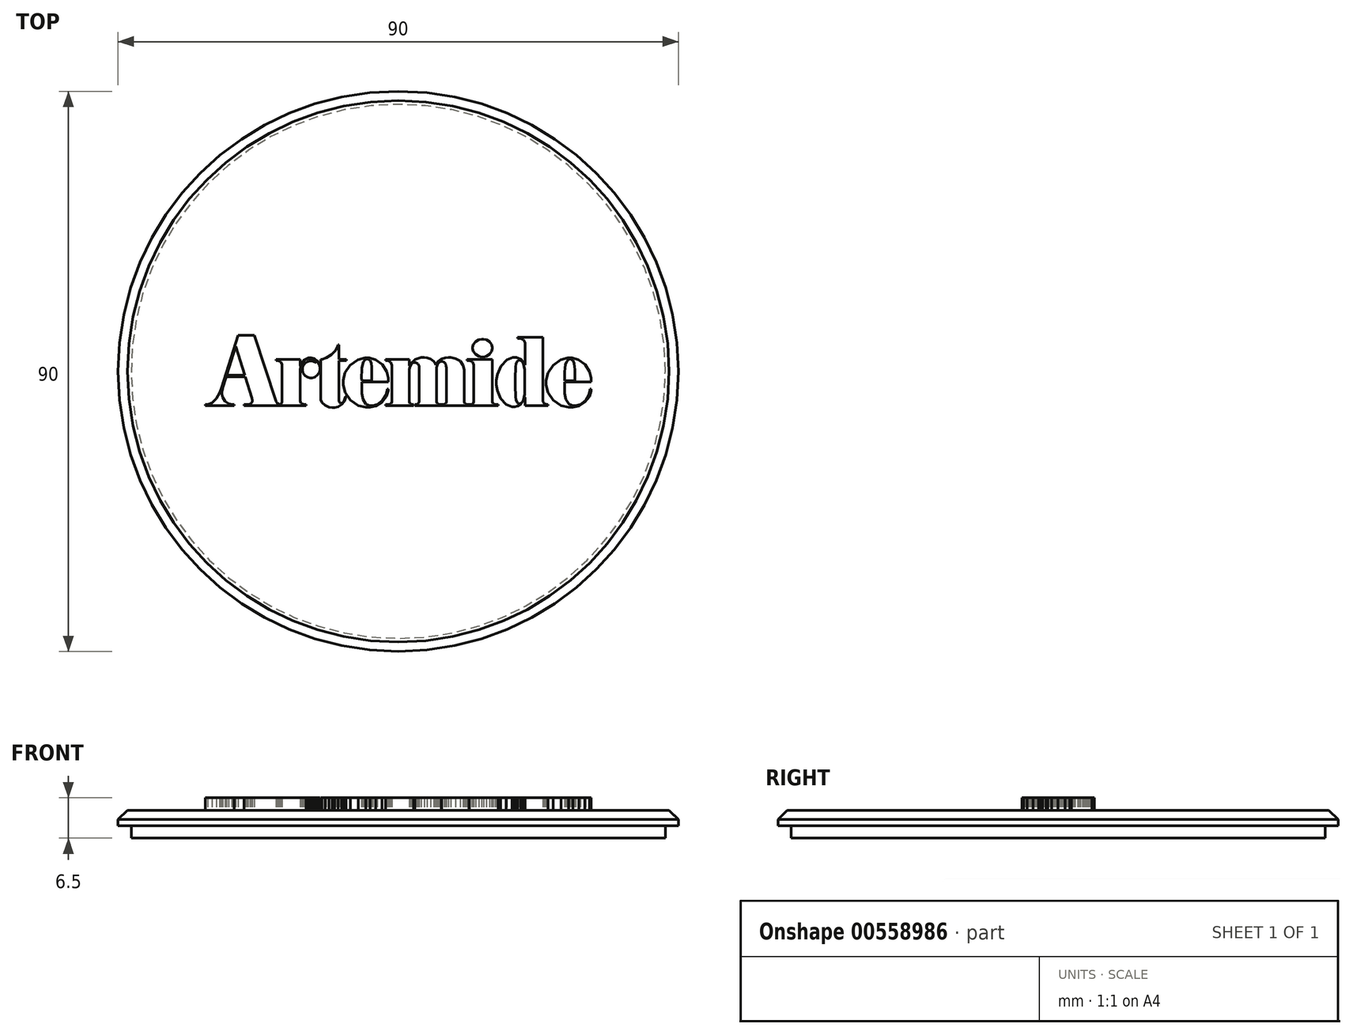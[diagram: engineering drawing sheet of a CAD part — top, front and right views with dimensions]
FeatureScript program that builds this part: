
annotation { "Feature Type Name" : "Feature", "Feature Type Description" : "" }
export const myFeature = defineFeature(function(context is Context, id is Id, definition is map)
    precondition{}
    {
        {
            var Q0;
            Q0=qCreatedBy(makeId("Top.planeOp"),FACE);
            var sketch = newSketch(context, id + "F0", { "sketchPlane" : qUnion([Q0])});
            skCircle(sketch, "E0", {"center": v(0, 0) * mm, "radius": 42.9 * mm});
            skSolve(sketch);
        }
        {
            var Q0;
            Q0 = qSketchRegion(id + "F0", true);
            extrude(context, id + "F1", {"entities" : qUnion([Q0]), "depth" : 2 * mm, "offsetDistance" : 25 * mm});
        }
        {
            var Q0;
            Q0=makeQuery(id+"F1.opExtrude","CAP_FACE",FACE,{"disambiguationData":[OSD([sQuery(id+"F0.wireOp",EDGE,"E0")])],"isStart":false});
            var sketch = newSketch(context, id + "F2", { "sketchPlane" : qUnion([Q0])});
            skCircle(sketch, "E1", {"center": v(0, 0) * mm, "radius": 45 * mm});
            skSolve(sketch);
        }
        {
            var Q0;
            Q0=makeQuery(id+"F2.imprint","IMPRINT",FACE,{"disambiguationData":[TD([[makeQuery(id+"F2.imprint","IMPRINT",EDGE,{"derivedFrom":sQuery(id+"F2.wireOp",EDGE,"E1")}),1.0]])]});
            var Q1;
            Q1=makeQuery(id+"F2.imprint","IMPRINT",FACE,{"disambiguationData":[TD([[makeQuery(id+"F2.imprint","IMPRINT",EDGE,{"derivedFrom":makeQuery(id+"F1.opExtrude","CAP_EDGE",EDGE,{"disambiguationData":[OSD([sQuery(id+"F0.wireOp",EDGE,"E0")])],"isStart":false})}),1.0]])]});
            extrude(context, id + "F3", {"entities" : qUnion([Q0, Q1]), "operationType" : NewBodyOperationType.ADD, "depth" : 2.5 * mm, "offsetDistance" : 25 * mm});
        }
        {
            var Q0;
            Q0=makeQuery(id+"F3.opExtrude","CAP_EDGE",EDGE,{"disambiguationData":[OSD([sQuery(id+"F2.wireOp",EDGE,"E1")])],"isStart":false});
            chamfer(context, id + "F4", {"entities" : qUnion([Q0]), "width" : 1.5 * mm, "tangentPropagation" : true});
        }
        {
            var Q0;
            Q0=makeQuery(id+"F3.opExtrude","CAP_FACE",FACE,{"disambiguationData":[OSD([sQuery(id+"F2.wireOp",EDGE,"E1")])],"isStart":false});
            var sketch = newSketch(context, id + "F5", { "sketchPlane" : qUnion([Q0])});
            skLineSegment(sketch, "E2", {"start": v(11.36, -5.33) * mm, "end": v(11.36, -5.52) * mm});
            skLineSegment(sketch, "E3", {"start": v(11.36, -5.52) * mm, "end": v(7, -5.52) * mm});
            skLineSegment(sketch, "E4", {"start": v(7, -5.52) * mm, "end": v(7, -5.33) * mm});
            skLineSegment(sketch, "E5", {"start": v(7, -5.33) * mm, "end": v(7.24, -5.33) * mm});
            skLineSegment(sketch, "E6", {"start": v(7.24, -5.33) * mm, "end": v(7.33, -5.33) * mm});
            skLineSegment(sketch, "E7", {"start": v(7.33, -5.33) * mm, "end": v(7.6, -5.2) * mm});
            skLineSegment(sketch, "E8", {"start": v(7.6, -5.2) * mm, "end": v(7.73, -4.93) * mm});
            skLineSegment(sketch, "E9", {"start": v(7.73, -4.93) * mm, "end": v(7.73, -4.84) * mm});
            skLineSegment(sketch, "E10", {"start": v(7.73, -4.84) * mm, "end": v(7.73, 0.46) * mm});
            skLineSegment(sketch, "E11", {"start": v(7.73, 0.46) * mm, "end": v(7.73, 0.56) * mm});
            skLineSegment(sketch, "E12", {"start": v(7.73, 0.56) * mm, "end": v(7.7, 0.85) * mm});
            skLineSegment(sketch, "E13", {"start": v(7.7, 0.85) * mm, "end": v(7.58, 1.21) * mm});
            skLineSegment(sketch, "E14", {"start": v(7.58, 1.21) * mm, "end": v(7.35, 1.48) * mm});
            skLineSegment(sketch, "E15", {"start": v(7.35, 1.48) * mm, "end": v(7.07, 1.58) * mm});
            skLineSegment(sketch, "E16", {"start": v(7.07, 1.58) * mm, "end": v(6.97, 1.58) * mm});
            skLineSegment(sketch, "E17", {"start": v(6.97, 1.58) * mm, "end": v(6.88, 1.58) * mm});
            skLineSegment(sketch, "E18", {"start": v(6.88, 1.58) * mm, "end": v(6.58, 1.48) * mm});
            skLineSegment(sketch, "E19", {"start": v(6.58, 1.48) * mm, "end": v(6.34, 1.21) * mm});
            skLineSegment(sketch, "E20", {"start": v(6.34, 1.21) * mm, "end": v(6.21, 0.85) * mm});
            skLineSegment(sketch, "E21", {"start": v(6.21, 0.85) * mm, "end": v(6.18, 0.56) * mm});
            skLineSegment(sketch, "E22", {"start": v(6.18, 0.56) * mm, "end": v(6.18, 0.46) * mm});
            skLineSegment(sketch, "E23", {"start": v(6.18, 0.46) * mm, "end": v(6.18, -4.74) * mm});
            skLineSegment(sketch, "E24", {"start": v(6.18, -4.74) * mm, "end": v(6.18, -4.85) * mm});
            skLineSegment(sketch, "E25", {"start": v(6.18, -4.85) * mm, "end": v(6.3, -5.17) * mm});
            skLineSegment(sketch, "E26", {"start": v(6.3, -5.17) * mm, "end": v(6.6, -5.33) * mm});
            skLineSegment(sketch, "E27", {"start": v(6.6, -5.33) * mm, "end": v(6.69, -5.33) * mm});
            skLineSegment(sketch, "E28", {"start": v(6.69, -5.33) * mm, "end": v(6.9, -5.33) * mm});
            skLineSegment(sketch, "E29", {"start": v(6.9, -5.33) * mm, "end": v(6.9, -5.52) * mm});
            skLineSegment(sketch, "E30", {"start": v(6.9, -5.52) * mm, "end": v(2.65, -5.52) * mm});
            skLineSegment(sketch, "E31", {"start": v(2.65, -5.52) * mm, "end": v(2.65, -5.33) * mm});
            skLineSegment(sketch, "E32", {"start": v(2.65, -5.33) * mm, "end": v(2.94, -5.33) * mm});
            skLineSegment(sketch, "E33", {"start": v(2.94, -5.33) * mm, "end": v(3.02, -5.33) * mm});
            skLineSegment(sketch, "E34", {"start": v(3.02, -5.33) * mm, "end": v(3.26, -5.14) * mm});
            skLineSegment(sketch, "E35", {"start": v(3.26, -5.14) * mm, "end": v(3.32, -4.84) * mm});
            skLineSegment(sketch, "E36", {"start": v(3.32, -4.84) * mm, "end": v(3.32, -4.74) * mm});
            skLineSegment(sketch, "E37", {"start": v(3.32, -4.74) * mm, "end": v(3.32, 0.68) * mm});
            skLineSegment(sketch, "E38", {"start": v(3.32, 0.68) * mm, "end": v(3.32, 0.81) * mm});
            skLineSegment(sketch, "E39", {"start": v(3.32, 0.81) * mm, "end": v(3.15, 1.2) * mm});
            skLineSegment(sketch, "E40", {"start": v(3.15, 1.2) * mm, "end": v(2.8, 1.44) * mm});
            skLineSegment(sketch, "E41", {"start": v(2.8, 1.44) * mm, "end": v(2.67, 1.44) * mm});
            skLineSegment(sketch, "E42", {"start": v(2.67, 1.44) * mm, "end": v(2.57, 1.44) * mm});
            skLineSegment(sketch, "E43", {"start": v(2.57, 1.44) * mm, "end": v(2.27, 1.32) * mm});
            skLineSegment(sketch, "E44", {"start": v(2.27, 1.32) * mm, "end": v(2, 1.01) * mm});
            skLineSegment(sketch, "E45", {"start": v(2, 1.01) * mm, "end": v(1.84, 0.61) * mm});
            skLineSegment(sketch, "E46", {"start": v(1.84, 0.61) * mm, "end": v(1.8, 0.3) * mm});
            skLineSegment(sketch, "E47", {"start": v(1.8, 0.3) * mm, "end": v(1.8, 0.2) * mm});
            skLineSegment(sketch, "E48", {"start": v(1.8, 0.2) * mm, "end": v(1.8, -4.74) * mm});
            skLineSegment(sketch, "E49", {"start": v(1.8, -4.74) * mm, "end": v(1.8, -4.85) * mm});
            skLineSegment(sketch, "E50", {"start": v(1.8, -4.85) * mm, "end": v(1.9, -5.16) * mm});
            skLineSegment(sketch, "E51", {"start": v(1.9, -5.16) * mm, "end": v(2.19, -5.33) * mm});
            skLineSegment(sketch, "E52", {"start": v(2.19, -5.33) * mm, "end": v(2.28, -5.33) * mm});
            skLineSegment(sketch, "E53", {"start": v(2.28, -5.33) * mm, "end": v(2.47, -5.33) * mm});
            skLineSegment(sketch, "E54", {"start": v(2.47, -5.33) * mm, "end": v(2.47, -5.52) * mm});
            skLineSegment(sketch, "E55", {"start": v(2.47, -5.52) * mm, "end": v(-2.02, -5.52) * mm});
            skLineSegment(sketch, "E56", {"start": v(-2.02, -5.52) * mm, "end": v(-2.02, -5.33) * mm});
            skLineSegment(sketch, "E57", {"start": v(-2.02, -5.33) * mm, "end": v(-1.57, -5.33) * mm});
            skLineSegment(sketch, "E58", {"start": v(-1.57, -5.33) * mm, "end": v(-1.46, -5.33) * mm});
            skLineSegment(sketch, "E59", {"start": v(-1.46, -5.33) * mm, "end": v(-1.13, -5.18) * mm});
            skLineSegment(sketch, "E60", {"start": v(-1.13, -5.18) * mm, "end": v(-1, -4.85) * mm});
            skLineSegment(sketch, "E61", {"start": v(-1, -4.85) * mm, "end": v(-1, -4.74) * mm});
            skLineSegment(sketch, "E62", {"start": v(-1, -4.74) * mm, "end": v(-1, 0.8) * mm});
            skLineSegment(sketch, "E63", {"start": v(-1, 0.8) * mm, "end": v(-1, 0.97) * mm});
            skLineSegment(sketch, "E64", {"start": v(-1, 0.97) * mm, "end": v(-1.2, 1.47) * mm});
            skLineSegment(sketch, "E65", {"start": v(-1.2, 1.47) * mm, "end": v(-1.66, 1.72) * mm});
            skLineSegment(sketch, "E66", {"start": v(-1.66, 1.72) * mm, "end": v(-1.82, 1.72) * mm});
            skLineSegment(sketch, "E67", {"start": v(-1.82, 1.72) * mm, "end": v(-2.02, 1.72) * mm});
            skLineSegment(sketch, "E68", {"start": v(-2.02, 1.72) * mm, "end": v(-2.02, 1.9) * mm});
            skLineSegment(sketch, "E69", {"start": v(-2.02, 1.9) * mm, "end": v(1.8, 1.9) * mm});
            skLineSegment(sketch, "E70", {"start": v(1.8, 1.9) * mm, "end": v(1.8, 0.93) * mm});
            skLineSegment(sketch, "E71", {"start": v(1.8, 0.93) * mm, "end": v(1.9, 1.15) * mm});
            skLineSegment(sketch, "E72", {"start": v(1.9, 1.15) * mm, "end": v(2.7, 1.9) * mm});
            skLineSegment(sketch, "E73", {"start": v(2.7, 1.9) * mm, "end": v(3.67, 2.21) * mm});
            skLineSegment(sketch, "E74", {"start": v(3.67, 2.21) * mm, "end": v(4, 2.21) * mm});
            skLineSegment(sketch, "E75", {"start": v(4, 2.21) * mm, "end": v(4.16, 2.21) * mm});
            skLineSegment(sketch, "E76", {"start": v(4.16, 2.21) * mm, "end": v(4.64, 2.16) * mm});
            skLineSegment(sketch, "E77", {"start": v(4.64, 2.16) * mm, "end": v(5.23, 1.97) * mm});
            skLineSegment(sketch, "E78", {"start": v(5.23, 1.97) * mm, "end": v(5.7, 1.61) * mm});
            skLineSegment(sketch, "E79", {"start": v(5.7, 1.61) * mm, "end": v(5.97, 1.2) * mm});
            skLineSegment(sketch, "E80", {"start": v(5.97, 1.2) * mm, "end": v(6.02, 1.05) * mm});
            skLineSegment(sketch, "E81", {"start": v(6.02, 1.05) * mm, "end": v(6.08, 1.2) * mm});
            skLineSegment(sketch, "E82", {"start": v(6.08, 1.2) * mm, "end": v(6.4, 1.6) * mm});
            skLineSegment(sketch, "E83", {"start": v(6.4, 1.6) * mm, "end": v(6.9, 1.96) * mm});
            skLineSegment(sketch, "E84", {"start": v(6.9, 1.96) * mm, "end": v(7.52, 2.16) * mm});
            skLineSegment(sketch, "E85", {"start": v(7.52, 2.16) * mm, "end": v(8.03, 2.21) * mm});
            skLineSegment(sketch, "E86", {"start": v(8.03, 2.21) * mm, "end": v(8.2, 2.21) * mm});
            skLineSegment(sketch, "E87", {"start": v(8.2, 2.21) * mm, "end": v(8.45, 2.21) * mm});
            skLineSegment(sketch, "E88", {"start": v(8.45, 2.21) * mm, "end": v(9.19, 2.08) * mm});
            skLineSegment(sketch, "E89", {"start": v(9.19, 2.08) * mm, "end": v(9.94, 1.67) * mm});
            skLineSegment(sketch, "E90", {"start": v(9.94, 1.67) * mm, "end": v(10.43, 0.98) * mm});
            skLineSegment(sketch, "E91", {"start": v(10.43, 0.98) * mm, "end": v(10.6, 0.25) * mm});
            skLineSegment(sketch, "E92", {"start": v(10.6, 0.25) * mm, "end": v(10.6, 0) * mm});
            skLineSegment(sketch, "E93", {"start": v(10.6, 0) * mm, "end": v(10.6, -4.84) * mm});
            skLineSegment(sketch, "E94", {"start": v(10.6, -4.84) * mm, "end": v(10.6, -4.93) * mm});
            skLineSegment(sketch, "E95", {"start": v(10.6, -4.93) * mm, "end": v(10.73, -5.18) * mm});
            skLineSegment(sketch, "E96", {"start": v(10.73, -5.18) * mm, "end": v(10.97, -5.33) * mm});
            skLineSegment(sketch, "E97", {"start": v(10.97, -5.33) * mm, "end": v(11.05, -5.33) * mm});
            skLineSegment(sketch, "E98", {"start": v(11.05, -5.33) * mm, "end": v(11.36, -5.33) * mm});
            skLineSegment(sketch, "E99", {"start": v(11.42, -5.33) * mm, "end": v(11.7, -5.33) * mm});
            skLineSegment(sketch, "E100", {"start": v(11.7, -5.33) * mm, "end": v(11.8, -5.33) * mm});
            skLineSegment(sketch, "E101", {"start": v(11.8, -5.33) * mm, "end": v(12.07, -5.12) * mm});
            skLineSegment(sketch, "E102", {"start": v(12.07, -5.12) * mm, "end": v(12.13, -4.79) * mm});
            skLineSegment(sketch, "E103", {"start": v(12.13, -4.79) * mm, "end": v(12.13, -4.68) * mm});
            skLineSegment(sketch, "E104", {"start": v(12.13, -4.68) * mm, "end": v(12.13, 0.85) * mm});
            skLineSegment(sketch, "E105", {"start": v(12.13, 0.85) * mm, "end": v(12.13, 1.02) * mm});
            skLineSegment(sketch, "E106", {"start": v(12.13, 1.02) * mm, "end": v(11.95, 1.52) * mm});
            skLineSegment(sketch, "E107", {"start": v(11.95, 1.52) * mm, "end": v(11.46, 1.72) * mm});
            skLineSegment(sketch, "E108", {"start": v(11.46, 1.72) * mm, "end": v(11.3, 1.72) * mm});
            skLineSegment(sketch, "E109", {"start": v(11.3, 1.72) * mm, "end": v(11.05, 1.72) * mm});
            skLineSegment(sketch, "E110", {"start": v(11.05, 1.72) * mm, "end": v(11.05, 1.9) * mm});
            skLineSegment(sketch, "E111", {"start": v(11.05, 1.9) * mm, "end": v(15.13, 1.9) * mm});
            skLineSegment(sketch, "E112", {"start": v(15.13, 1.9) * mm, "end": v(15.13, -4.74) * mm});
            skLineSegment(sketch, "E113", {"start": v(15.13, -4.74) * mm, "end": v(15.13, -4.85) * mm});
            skLineSegment(sketch, "E114", {"start": v(15.13, -4.85) * mm, "end": v(15.25, -5.17) * mm});
            skLineSegment(sketch, "E115", {"start": v(15.25, -5.17) * mm, "end": v(15.56, -5.33) * mm});
            skLineSegment(sketch, "E116", {"start": v(15.56, -5.33) * mm, "end": v(15.66, -5.33) * mm});
            skLineSegment(sketch, "E117", {"start": v(15.66, -5.33) * mm, "end": v(16.07, -5.33) * mm});
            skLineSegment(sketch, "E118", {"start": v(16.07, -5.33) * mm, "end": v(16.07, -5.52) * mm});
            skLineSegment(sketch, "E119", {"start": v(16.07, -5.52) * mm, "end": v(11.42, -5.52) * mm});
            skLineSegment(sketch, "E120", {"start": v(11.42, -5.52) * mm, "end": v(11.42, -5.33) * mm});
            skLineSegment(sketch, "E121", {"start": v(-12.48, 1.9) * mm, "end": v(-12.25, 1.95) * mm});
            skLineSegment(sketch, "E122", {"start": v(-12.25, 1.95) * mm, "end": v(-11.57, 2.2) * mm});
            skLineSegment(sketch, "E123", {"start": v(-11.57, 2.2) * mm, "end": v(-10.73, 2.7) * mm});
            skLineSegment(sketch, "E124", {"start": v(-10.73, 2.7) * mm, "end": v(-10.06, 3.4) * mm});
            skLineSegment(sketch, "E125", {"start": v(-10.06, 3.4) * mm, "end": v(-9.74, 4.06) * mm});
            skLineSegment(sketch, "E126", {"start": v(-9.74, 4.06) * mm, "end": v(-9.69, 4.3) * mm});
            skLineSegment(sketch, "E127", {"start": v(-9.69, 4.3) * mm, "end": v(-9.55, 4.3) * mm});
            skLineSegment(sketch, "E128", {"start": v(-9.55, 4.3) * mm, "end": v(-9.55, 1.9) * mm});
            skLineSegment(sketch, "E129", {"start": v(-9.55, 1.9) * mm, "end": v(-8.3, 1.9) * mm});
            skLineSegment(sketch, "E130", {"start": v(-8.3, 1.9) * mm, "end": v(-8.3, 1.72) * mm});
            skLineSegment(sketch, "E131", {"start": v(-8.3, 1.72) * mm, "end": v(-9.55, 1.72) * mm});
            skLineSegment(sketch, "E132", {"start": v(-9.55, 1.72) * mm, "end": v(-9.55, -4.6) * mm});
            skLineSegment(sketch, "E133", {"start": v(-9.55, -4.6) * mm, "end": v(-9.55, -4.69) * mm});
            skLineSegment(sketch, "E134", {"start": v(-9.55, -4.69) * mm, "end": v(-9.48, -4.95) * mm});
            skLineSegment(sketch, "E135", {"start": v(-9.48, -4.95) * mm, "end": v(-9.27, -5.13) * mm});
            skLineSegment(sketch, "E136", {"start": v(-9.27, -5.13) * mm, "end": v(-9.2, -5.13) * mm});
            skLineSegment(sketch, "E137", {"start": v(-9.2, -5.13) * mm, "end": v(-9.13, -5.13) * mm});
            skLineSegment(sketch, "E138", {"start": v(-9.13, -5.13) * mm, "end": v(-8.9, -5.01) * mm});
            skLineSegment(sketch, "E139", {"start": v(-8.9, -5.01) * mm, "end": v(-8.72, -4.73) * mm});
            skLineSegment(sketch, "E140", {"start": v(-8.72, -4.73) * mm, "end": v(-8.6, -4.38) * mm});
            skLineSegment(sketch, "E141", {"start": v(-8.6, -4.38) * mm, "end": v(-8.54, -4.15) * mm});
            skLineSegment(sketch, "E142", {"start": v(-8.54, -4.15) * mm, "end": v(-8.53, -4.07) * mm});
            skLineSegment(sketch, "E143", {"start": v(-8.53, -4.07) * mm, "end": v(-8.4, -4.07) * mm});
            skLineSegment(sketch, "E144", {"start": v(-8.4, -4.07) * mm, "end": v(-8.44, -4.25) * mm});
            skLineSegment(sketch, "E145", {"start": v(-8.44, -4.25) * mm, "end": v(-8.65, -4.78) * mm});
            skLineSegment(sketch, "E146", {"start": v(-8.65, -4.78) * mm, "end": v(-9.07, -5.33) * mm});
            skLineSegment(sketch, "E147", {"start": v(-9.07, -5.33) * mm, "end": v(-9.66, -5.7) * mm});
            skLineSegment(sketch, "E148", {"start": v(-9.66, -5.7) * mm, "end": v(-10.23, -5.82) * mm});
            skLineSegment(sketch, "E149", {"start": v(-10.23, -5.82) * mm, "end": v(-10.42, -5.82) * mm});
            skLineSegment(sketch, "E150", {"start": v(-10.42, -5.82) * mm, "end": v(-10.6, -5.82) * mm});
            skLineSegment(sketch, "E151", {"start": v(-10.6, -5.82) * mm, "end": v(-11.1, -5.73) * mm});
            skLineSegment(sketch, "E152", {"start": v(-11.1, -5.73) * mm, "end": v(-11.77, -5.47) * mm});
            skLineSegment(sketch, "E153", {"start": v(-11.77, -5.47) * mm, "end": v(-12.28, -5.01) * mm});
            skLineSegment(sketch, "E154", {"start": v(-12.28, -5.01) * mm, "end": v(-12.48, -4.53) * mm});
            skLineSegment(sketch, "E155", {"start": v(-12.48, -4.53) * mm, "end": v(-12.48, -4.38) * mm});
            skLineSegment(sketch, "E156", {"start": v(-12.48, -4.38) * mm, "end": v(-12.48, 1.9) * mm});
            skLineSegment(sketch, "E157", {"start": v(-13.13, 1.38) * mm, "end": v(-13.18, 1.5) * mm});
            skLineSegment(sketch, "E158", {"start": v(-13.18, 1.5) * mm, "end": v(-13.55, 1.9) * mm});
            skLineSegment(sketch, "E159", {"start": v(-13.55, 1.9) * mm, "end": v(-14.03, 2.07) * mm});
            skLineSegment(sketch, "E160", {"start": v(-14.03, 2.07) * mm, "end": v(-14.2, 2.07) * mm});
            skLineSegment(sketch, "E161", {"start": v(-14.2, 2.07) * mm, "end": v(-14.37, 2.07) * mm});
            skLineSegment(sketch, "E162", {"start": v(-14.37, 2.07) * mm, "end": v(-14.9, 1.9) * mm});
            skLineSegment(sketch, "E163", {"start": v(-14.9, 1.9) * mm, "end": v(-15.39, 1.44) * mm});
            skLineSegment(sketch, "E164", {"start": v(-15.39, 1.44) * mm, "end": v(-15.69, 0.8) * mm});
            skLineSegment(sketch, "E165", {"start": v(-15.69, 0.8) * mm, "end": v(-15.79, 0.27) * mm});
            skLineSegment(sketch, "E166", {"start": v(-15.79, 0.27) * mm, "end": v(-15.79, 0.1) * mm});
            skLineSegment(sketch, "E167", {"start": v(-15.79, 0.1) * mm, "end": v(-15.79, -4.58) * mm});
            skLineSegment(sketch, "E168", {"start": v(-15.79, -4.58) * mm, "end": v(-15.79, -4.71) * mm});
            skLineSegment(sketch, "E169", {"start": v(-15.79, -4.71) * mm, "end": v(-15.6, -5.12) * mm});
            skLineSegment(sketch, "E170", {"start": v(-15.6, -5.12) * mm, "end": v(-15.2, -5.33) * mm});
            skLineSegment(sketch, "E171", {"start": v(-15.2, -5.33) * mm, "end": v(-15.07, -5.33) * mm});
            skLineSegment(sketch, "E172", {"start": v(-15.07, -5.33) * mm, "end": v(-14.79, -5.33) * mm});
            skLineSegment(sketch, "E173", {"start": v(-14.79, -5.33) * mm, "end": v(-14.79, -5.52) * mm});
            skLineSegment(sketch, "E174", {"start": v(-14.79, -5.52) * mm, "end": v(-24.8, -5.52) * mm});
            skLineSegment(sketch, "E175", {"start": v(-24.8, -5.52) * mm, "end": v(-24.8, -5.33) * mm});
            skLineSegment(sketch, "E176", {"start": v(-24.8, -5.33) * mm, "end": v(-24.47, -5.33) * mm});
            skLineSegment(sketch, "E177", {"start": v(-24.47, -5.33) * mm, "end": v(-24.4, -5.33) * mm});
            skLineSegment(sketch, "E178", {"start": v(-24.4, -5.33) * mm, "end": v(-24.16, -5.31) * mm});
            skLineSegment(sketch, "E179", {"start": v(-24.16, -5.31) * mm, "end": v(-23.82, -5.24) * mm});
            skLineSegment(sketch, "E180", {"start": v(-23.82, -5.24) * mm, "end": v(-23.55, -5.07) * mm});
            skLineSegment(sketch, "E181", {"start": v(-23.55, -5.07) * mm, "end": v(-23.43, -4.84) * mm});
            skLineSegment(sketch, "E182", {"start": v(-23.43, -4.84) * mm, "end": v(-23.43, -4.76) * mm});
            skLineSegment(sketch, "E183", {"start": v(-23.43, -4.76) * mm, "end": v(-23.43, -4.65) * mm});
            skLineSegment(sketch, "E184", {"start": v(-23.43, -4.65) * mm, "end": v(-23.5, -4.35) * mm});
            skLineSegment(sketch, "E185", {"start": v(-23.5, -4.35) * mm, "end": v(-23.52, -4.31) * mm});
            skLineSegment(sketch, "E186", {"start": v(-23.52, -4.31) * mm, "end": v(-24.6, -0.85) * mm});
            skLineSegment(sketch, "E187", {"start": v(-24.6, -0.85) * mm, "end": v(-27.62, -0.85) * mm});
            skLineSegment(sketch, "E188", {"start": v(-27.62, -0.85) * mm, "end": v(-28.19, -2.66) * mm});
            skLineSegment(sketch, "E189", {"start": v(-28.19, -2.66) * mm, "end": v(-28.2, -2.73) * mm});
            skLineSegment(sketch, "E190", {"start": v(-28.2, -2.73) * mm, "end": v(-28.3, -3.29) * mm});
            skLineSegment(sketch, "E191", {"start": v(-28.3, -3.29) * mm, "end": v(-28.3, -3.48) * mm});
            skLineSegment(sketch, "E192", {"start": v(-28.3, -3.48) * mm, "end": v(-28.3, -3.66) * mm});
            skLineSegment(sketch, "E193", {"start": v(-28.3, -3.66) * mm, "end": v(-28.18, -4.2) * mm});
            skLineSegment(sketch, "E194", {"start": v(-28.18, -4.2) * mm, "end": v(-27.83, -4.8) * mm});
            skLineSegment(sketch, "E195", {"start": v(-27.83, -4.8) * mm, "end": v(-27.28, -5.19) * mm});
            skLineSegment(sketch, "E196", {"start": v(-27.28, -5.19) * mm, "end": v(-26.73, -5.33) * mm});
            skLineSegment(sketch, "E197", {"start": v(-26.73, -5.33) * mm, "end": v(-26.55, -5.33) * mm});
            skLineSegment(sketch, "E198", {"start": v(-26.55, -5.33) * mm, "end": v(-26.37, -5.33) * mm});
            skLineSegment(sketch, "E199", {"start": v(-26.37, -5.33) * mm, "end": v(-26.37, -5.52) * mm});
            skLineSegment(sketch, "E200", {"start": v(-26.37, -5.52) * mm, "end": v(-31, -5.52) * mm});
            skLineSegment(sketch, "E201", {"start": v(-31, -5.52) * mm, "end": v(-31, -5.33) * mm});
            skLineSegment(sketch, "E202", {"start": v(-31, -5.33) * mm, "end": v(-30.82, -5.33) * mm});
            skLineSegment(sketch, "E203", {"start": v(-30.82, -5.33) * mm, "end": v(-30.6, -5.33) * mm});
            skLineSegment(sketch, "E204", {"start": v(-30.6, -5.33) * mm, "end": v(-29.91, -5.06) * mm});
            skLineSegment(sketch, "E205", {"start": v(-29.91, -5.06) * mm, "end": v(-29.22, -4.38) * mm});
            skLineSegment(sketch, "E206", {"start": v(-29.22, -4.38) * mm, "end": v(-28.72, -3.5) * mm});
            skLineSegment(sketch, "E207", {"start": v(-28.72, -3.5) * mm, "end": v(-28.46, -2.84) * mm});
            skLineSegment(sketch, "E208", {"start": v(-28.46, -2.84) * mm, "end": v(-28.39, -2.62) * mm});
            skLineSegment(sketch, "E209", {"start": v(-28.39, -2.62) * mm, "end": v(-25.74, 5.82) * mm});
            skLineSegment(sketch, "E210", {"start": v(-25.74, 5.82) * mm, "end": v(-23.1, 5.82) * mm});
            skLineSegment(sketch, "E211", {"start": v(-23.1, 5.82) * mm, "end": v(-19.64, -4.78) * mm});
            skLineSegment(sketch, "E212", {"start": v(-19.64, -4.78) * mm, "end": v(-19.62, -4.84) * mm});
            skLineSegment(sketch, "E213", {"start": v(-19.62, -4.84) * mm, "end": v(-19.42, -5.13) * mm});
            skLineSegment(sketch, "E214", {"start": v(-19.42, -5.13) * mm, "end": v(-19.14, -5.3) * mm});
            skLineSegment(sketch, "E215", {"start": v(-19.14, -5.3) * mm, "end": v(-19.05, -5.3) * mm});
            skLineSegment(sketch, "E216", {"start": v(-19.05, -5.3) * mm, "end": v(-18.98, -5.3) * mm});
            skLineSegment(sketch, "E217", {"start": v(-18.98, -5.3) * mm, "end": v(-18.76, -5.12) * mm});
            skLineSegment(sketch, "E218", {"start": v(-18.76, -5.12) * mm, "end": v(-18.68, -4.87) * mm});
            skLineSegment(sketch, "E219", {"start": v(-18.68, -4.87) * mm, "end": v(-18.68, -4.78) * mm});
            skLineSegment(sketch, "E220", {"start": v(-18.68, -4.78) * mm, "end": v(-18.68, 0.93) * mm});
            skLineSegment(sketch, "E221", {"start": v(-18.68, 0.93) * mm, "end": v(-18.68, 1.08) * mm});
            skLineSegment(sketch, "E222", {"start": v(-18.68, 1.08) * mm, "end": v(-18.86, 1.53) * mm});
            skLineSegment(sketch, "E223", {"start": v(-18.86, 1.53) * mm, "end": v(-19.3, 1.72) * mm});
            skLineSegment(sketch, "E224", {"start": v(-19.3, 1.72) * mm, "end": v(-19.44, 1.72) * mm});
            skLineSegment(sketch, "E225", {"start": v(-19.44, 1.72) * mm, "end": v(-19.64, 1.72) * mm});
            skLineSegment(sketch, "E226", {"start": v(-19.64, 1.72) * mm, "end": v(-19.64, 1.9) * mm});
            skLineSegment(sketch, "E227", {"start": v(-19.64, 1.9) * mm, "end": v(-15.79, 1.9) * mm});
            skLineSegment(sketch, "E228", {"start": v(-15.79, 1.9) * mm, "end": v(-15.79, 0.89) * mm});
            skLineSegment(sketch, "E229", {"start": v(-15.79, 0.89) * mm, "end": v(-15.73, 1.07) * mm});
            skLineSegment(sketch, "E230", {"start": v(-15.73, 1.07) * mm, "end": v(-15.17, 1.82) * mm});
            skLineSegment(sketch, "E231", {"start": v(-15.17, 1.82) * mm, "end": v(-14.4, 2.2) * mm});
            skLineSegment(sketch, "E232", {"start": v(-14.4, 2.2) * mm, "end": v(-14.13, 2.2) * mm});
            skLineSegment(sketch, "E233", {"start": v(-14.13, 2.2) * mm, "end": v(-13.98, 2.2) * mm});
            skLineSegment(sketch, "E234", {"start": v(-13.98, 2.2) * mm, "end": v(-13.5, 2.05) * mm});
            skLineSegment(sketch, "E235", {"start": v(-13.5, 2.05) * mm, "end": v(-13, 1.69) * mm});
            skLineSegment(sketch, "E236", {"start": v(-13, 1.69) * mm, "end": v(-12.68, 1.15) * mm});
            skLineSegment(sketch, "E237", {"start": v(-12.68, 1.15) * mm, "end": v(-12.56, 0.68) * mm});
            skLineSegment(sketch, "E238", {"start": v(-12.56, 0.68) * mm, "end": v(-12.56, 0.52) * mm});
            skLineSegment(sketch, "E239", {"start": v(-12.56, 0.52) * mm, "end": v(-12.56, 0.37) * mm});
            skLineSegment(sketch, "E240", {"start": v(-12.56, 0.37) * mm, "end": v(-12.67, -0.09) * mm});
            skLineSegment(sketch, "E241", {"start": v(-12.67, -0.09) * mm, "end": v(-12.96, -0.59) * mm});
            skLineSegment(sketch, "E242", {"start": v(-12.96, -0.59) * mm, "end": v(-13.42, -0.92) * mm});
            skLineSegment(sketch, "E243", {"start": v(-13.42, -0.92) * mm, "end": v(-13.88, -1.05) * mm});
            skLineSegment(sketch, "E244", {"start": v(-13.88, -1.05) * mm, "end": v(-14.03, -1.05) * mm});
            skLineSegment(sketch, "E245", {"start": v(-14.03, -1.05) * mm, "end": v(-14.17, -1.05) * mm});
            skLineSegment(sketch, "E246", {"start": v(-14.17, -1.05) * mm, "end": v(-14.57, -0.95) * mm});
            skLineSegment(sketch, "E247", {"start": v(-14.57, -0.95) * mm, "end": v(-15, -0.66) * mm});
            skLineSegment(sketch, "E248", {"start": v(-15, -0.66) * mm, "end": v(-15.3, -0.22) * mm});
            skLineSegment(sketch, "E249", {"start": v(-15.3, -0.22) * mm, "end": v(-15.4, 0.18) * mm});
            skLineSegment(sketch, "E250", {"start": v(-15.4, 0.18) * mm, "end": v(-15.4, 0.32) * mm});
            skLineSegment(sketch, "E251", {"start": v(-15.4, 0.32) * mm, "end": v(-15.4, 0.45) * mm});
            skLineSegment(sketch, "E252", {"start": v(-15.4, 0.45) * mm, "end": v(-15.3, 0.86) * mm});
            skLineSegment(sketch, "E253", {"start": v(-15.3, 0.86) * mm, "end": v(-15.02, 1.29) * mm});
            skLineSegment(sketch, "E254", {"start": v(-15.02, 1.29) * mm, "end": v(-14.6, 1.56) * mm});
            skLineSegment(sketch, "E255", {"start": v(-14.6, 1.56) * mm, "end": v(-14.19, 1.66) * mm});
            skLineSegment(sketch, "E256", {"start": v(-14.19, 1.66) * mm, "end": v(-14.05, 1.66) * mm});
            skLineSegment(sketch, "E257", {"start": v(-14.05, 1.66) * mm, "end": v(-13.82, 1.66) * mm});
            skLineSegment(sketch, "E258", {"start": v(-13.82, 1.66) * mm, "end": v(-13.2, 1.42) * mm});
            skLineSegment(sketch, "E259", {"start": v(-13.2, 1.42) * mm, "end": v(-13.13, 1.38) * mm});
            skLineSegment(sketch, "E260", {"start": v(-1.61, -1.68) * mm, "end": v(-5.85, -1.68) * mm});
            skLineSegment(sketch, "E261", {"start": v(-5.85, -1.68) * mm, "end": v(-5.86, -1.76) * mm});
            skLineSegment(sketch, "E262", {"start": v(-5.86, -1.76) * mm, "end": v(-5.87, -2.44) * mm});
            skLineSegment(sketch, "E263", {"start": v(-5.87, -2.44) * mm, "end": v(-5.87, -2.66) * mm});
            skLineSegment(sketch, "E264", {"start": v(-5.87, -2.66) * mm, "end": v(-5.87, -2.88) * mm});
            skLineSegment(sketch, "E265", {"start": v(-5.87, -2.88) * mm, "end": v(-5.85, -3.56) * mm});
            skLineSegment(sketch, "E266", {"start": v(-5.85, -3.56) * mm, "end": v(-5.67, -4.5) * mm});
            skLineSegment(sketch, "E267", {"start": v(-5.67, -4.5) * mm, "end": v(-5.21, -5.24) * mm});
            skLineSegment(sketch, "E268", {"start": v(-5.21, -5.24) * mm, "end": v(-4.56, -5.54) * mm});
            skLineSegment(sketch, "E269", {"start": v(-4.56, -5.54) * mm, "end": v(-4.34, -5.54) * mm});
            skLineSegment(sketch, "E270", {"start": v(-4.34, -5.54) * mm, "end": v(-4.1, -5.54) * mm});
            skLineSegment(sketch, "E271", {"start": v(-4.1, -5.54) * mm, "end": v(-3.34, -5.3) * mm});
            skLineSegment(sketch, "E272", {"start": v(-3.34, -5.3) * mm, "end": v(-2.53, -4.69) * mm});
            skLineSegment(sketch, "E273", {"start": v(-2.53, -4.69) * mm, "end": v(-1.99, -3.82) * mm});
            skLineSegment(sketch, "E274", {"start": v(-1.99, -3.82) * mm, "end": v(-1.78, -3.07) * mm});
            skLineSegment(sketch, "E275", {"start": v(-1.78, -3.07) * mm, "end": v(-1.77, -2.82) * mm});
            skLineSegment(sketch, "E276", {"start": v(-1.77, -2.82) * mm, "end": v(-1.61, -2.82) * mm});
            skLineSegment(sketch, "E277", {"start": v(-1.61, -2.82) * mm, "end": v(-1.62, -3.12) * mm});
            skLineSegment(sketch, "E278", {"start": v(-1.62, -3.12) * mm, "end": v(-1.9, -4.02) * mm});
            skLineSegment(sketch, "E279", {"start": v(-1.9, -4.02) * mm, "end": v(-2.6, -4.95) * mm});
            skLineSegment(sketch, "E280", {"start": v(-2.6, -4.95) * mm, "end": v(-3.61, -5.56) * mm});
            skLineSegment(sketch, "E281", {"start": v(-3.61, -5.56) * mm, "end": v(-4.53, -5.78) * mm});
            skLineSegment(sketch, "E282", {"start": v(-4.53, -5.78) * mm, "end": v(-4.83, -5.78) * mm});
            skLineSegment(sketch, "E283", {"start": v(-4.83, -5.78) * mm, "end": v(-5.23, -5.78) * mm});
            skLineSegment(sketch, "E284", {"start": v(-5.23, -5.78) * mm, "end": v(-6.42, -5.48) * mm});
            skLineSegment(sketch, "E285", {"start": v(-6.42, -5.48) * mm, "end": v(-7.7, -4.64) * mm});
            skLineSegment(sketch, "E286", {"start": v(-7.7, -4.64) * mm, "end": v(-8.54, -3.38) * mm});
            skLineSegment(sketch, "E287", {"start": v(-8.54, -3.38) * mm, "end": v(-8.85, -2.2) * mm});
            skLineSegment(sketch, "E288", {"start": v(-8.85, -2.2) * mm, "end": v(-8.85, -1.8) * mm});
            skLineSegment(sketch, "E289", {"start": v(-8.85, -1.8) * mm, "end": v(-8.85, -1.42) * mm});
            skLineSegment(sketch, "E290", {"start": v(-8.85, -1.42) * mm, "end": v(-8.56, -0.27) * mm});
            skLineSegment(sketch, "E291", {"start": v(-8.56, -0.27) * mm, "end": v(-7.74, 1) * mm});
            skLineSegment(sketch, "E292", {"start": v(-7.74, 1) * mm, "end": v(-6.51, 1.84) * mm});
            skLineSegment(sketch, "E293", {"start": v(-6.51, 1.84) * mm, "end": v(-5.36, 2.15) * mm});
            skLineSegment(sketch, "E294", {"start": v(-5.36, 2.15) * mm, "end": v(-4.98, 2.15) * mm});
            skLineSegment(sketch, "E295", {"start": v(-4.98, 2.15) * mm, "end": v(-4.64, 2.15) * mm});
            skLineSegment(sketch, "E296", {"start": v(-4.64, 2.15) * mm, "end": v(-3.61, 1.87) * mm});
            skLineSegment(sketch, "E297", {"start": v(-3.61, 1.87) * mm, "end": v(-2.54, 1.1) * mm});
            skLineSegment(sketch, "E298", {"start": v(-2.54, 1.1) * mm, "end": v(-1.84, -0.03) * mm});
            skLineSegment(sketch, "E299", {"start": v(-1.84, -0.03) * mm, "end": v(-1.6, -1.06) * mm});
            skLineSegment(sketch, "E300", {"start": v(-1.6, -1.06) * mm, "end": v(-1.6, -1.4) * mm});
            skLineSegment(sketch, "E301", {"start": v(-1.6, -1.4) * mm, "end": v(-1.6, -1.47) * mm});
            skLineSegment(sketch, "E302", {"start": v(-1.6, -1.47) * mm, "end": v(-1.61, -1.63) * mm});
            skLineSegment(sketch, "E303", {"start": v(-1.61, -1.63) * mm, "end": v(-1.61, -1.68) * mm});
            skLineSegment(sketch, "E304", {"start": v(20.35, 1.05) * mm, "end": v(20.35, 4.46) * mm});
            skLineSegment(sketch, "E305", {"start": v(20.35, 4.46) * mm, "end": v(20.35, 4.61) * mm});
            skLineSegment(sketch, "E306", {"start": v(20.35, 4.61) * mm, "end": v(20.11, 5.08) * mm});
            skLineSegment(sketch, "E307", {"start": v(20.11, 5.08) * mm, "end": v(19.62, 5.27) * mm});
            skLineSegment(sketch, "E308", {"start": v(19.62, 5.27) * mm, "end": v(19.46, 5.27) * mm});
            skLineSegment(sketch, "E309", {"start": v(19.46, 5.27) * mm, "end": v(19.17, 5.27) * mm});
            skLineSegment(sketch, "E310", {"start": v(19.17, 5.27) * mm, "end": v(19.17, 5.46) * mm});
            skLineSegment(sketch, "E311", {"start": v(19.17, 5.46) * mm, "end": v(23.25, 5.46) * mm});
            skLineSegment(sketch, "E312", {"start": v(23.25, 5.46) * mm, "end": v(23.25, -4.74) * mm});
            skLineSegment(sketch, "E313", {"start": v(23.25, -4.74) * mm, "end": v(23.25, -4.86) * mm});
            skLineSegment(sketch, "E314", {"start": v(23.25, -4.86) * mm, "end": v(23.47, -5.21) * mm});
            skLineSegment(sketch, "E315", {"start": v(23.47, -5.21) * mm, "end": v(23.87, -5.33) * mm});
            skLineSegment(sketch, "E316", {"start": v(23.87, -5.33) * mm, "end": v(24, -5.33) * mm});
            skLineSegment(sketch, "E317", {"start": v(24, -5.33) * mm, "end": v(24.04, -5.33) * mm});
            skLineSegment(sketch, "E318", {"start": v(24.04, -5.33) * mm, "end": v(24.04, -5.52) * mm});
            skLineSegment(sketch, "E319", {"start": v(24.04, -5.52) * mm, "end": v(20.35, -5.52) * mm});
            skLineSegment(sketch, "E320", {"start": v(20.35, -5.52) * mm, "end": v(20.35, -4.17) * mm});
            skLineSegment(sketch, "E321", {"start": v(20.35, -4.17) * mm, "end": v(20.3, -4.32) * mm});
            skLineSegment(sketch, "E322", {"start": v(20.3, -4.32) * mm, "end": v(20.07, -4.74) * mm});
            skLineSegment(sketch, "E323", {"start": v(20.07, -4.74) * mm, "end": v(19.7, -5.23) * mm});
            skLineSegment(sketch, "E324", {"start": v(19.7, -5.23) * mm, "end": v(19.2, -5.57) * mm});
            skLineSegment(sketch, "E325", {"start": v(19.2, -5.57) * mm, "end": v(18.72, -5.7) * mm});
            skLineSegment(sketch, "E326", {"start": v(18.72, -5.7) * mm, "end": v(18.56, -5.7) * mm});
            skLineSegment(sketch, "E327", {"start": v(18.56, -5.7) * mm, "end": v(18.25, -5.7) * mm});
            skLineSegment(sketch, "E328", {"start": v(18.25, -5.7) * mm, "end": v(17.31, -5.32) * mm});
            skLineSegment(sketch, "E329", {"start": v(17.31, -5.32) * mm, "end": v(16.44, -4.36) * mm});
            skLineSegment(sketch, "E330", {"start": v(16.44, -4.36) * mm, "end": v(15.93, -3.1) * mm});
            skLineSegment(sketch, "E331", {"start": v(15.93, -3.1) * mm, "end": v(15.77, -2.13) * mm});
            skLineSegment(sketch, "E332", {"start": v(15.77, -2.13) * mm, "end": v(15.77, -1.8) * mm});
            skLineSegment(sketch, "E333", {"start": v(15.77, -1.8) * mm, "end": v(15.77, -1.47) * mm});
            skLineSegment(sketch, "E334", {"start": v(15.77, -1.47) * mm, "end": v(15.96, -0.47) * mm});
            skLineSegment(sketch, "E335", {"start": v(15.96, -0.47) * mm, "end": v(16.52, 0.84) * mm});
            skLineSegment(sketch, "E336", {"start": v(16.52, 0.84) * mm, "end": v(17.46, 1.84) * mm});
            skLineSegment(sketch, "E337", {"start": v(17.46, 1.84) * mm, "end": v(18.44, 2.23) * mm});
            skLineSegment(sketch, "E338", {"start": v(18.44, 2.23) * mm, "end": v(18.76, 2.23) * mm});
            skLineSegment(sketch, "E339", {"start": v(18.76, 2.23) * mm, "end": v(19, 2.23) * mm});
            skLineSegment(sketch, "E340", {"start": v(19, 2.23) * mm, "end": v(19.75, 1.9) * mm});
            skLineSegment(sketch, "E341", {"start": v(19.75, 1.9) * mm, "end": v(20.28, 1.22) * mm});
            skLineSegment(sketch, "E342", {"start": v(20.28, 1.22) * mm, "end": v(20.35, 1.05) * mm});
            skLineSegment(sketch, "E343", {"start": v(13.54, 5.19) * mm, "end": v(13.69, 5.19) * mm});
            skLineSegment(sketch, "E344", {"start": v(13.69, 5.19) * mm, "end": v(14.13, 5.08) * mm});
            skLineSegment(sketch, "E345", {"start": v(14.13, 5.08) * mm, "end": v(14.64, 4.79) * mm});
            skLineSegment(sketch, "E346", {"start": v(14.64, 4.79) * mm, "end": v(15, 4.34) * mm});
            skLineSegment(sketch, "E347", {"start": v(15, 4.34) * mm, "end": v(15.13, 3.9) * mm});
            skLineSegment(sketch, "E348", {"start": v(15.13, 3.9) * mm, "end": v(15.13, 3.76) * mm});
            skLineSegment(sketch, "E349", {"start": v(15.13, 3.76) * mm, "end": v(15.13, 3.62) * mm});
            skLineSegment(sketch, "E350", {"start": v(15.13, 3.62) * mm, "end": v(15, 3.18) * mm});
            skLineSegment(sketch, "E351", {"start": v(15, 3.18) * mm, "end": v(14.64, 2.72) * mm});
            skLineSegment(sketch, "E352", {"start": v(14.64, 2.72) * mm, "end": v(14.13, 2.42) * mm});
            skLineSegment(sketch, "E353", {"start": v(14.13, 2.42) * mm, "end": v(13.69, 2.32) * mm});
            skLineSegment(sketch, "E354", {"start": v(13.69, 2.32) * mm, "end": v(13.54, 2.32) * mm});
            skLineSegment(sketch, "E355", {"start": v(13.54, 2.32) * mm, "end": v(13.4, 2.32) * mm});
            skLineSegment(sketch, "E356", {"start": v(13.4, 2.32) * mm, "end": v(12.94, 2.42) * mm});
            skLineSegment(sketch, "E357", {"start": v(12.94, 2.42) * mm, "end": v(12.43, 2.72) * mm});
            skLineSegment(sketch, "E358", {"start": v(12.43, 2.72) * mm, "end": v(12.07, 3.18) * mm});
            skLineSegment(sketch, "E359", {"start": v(12.07, 3.18) * mm, "end": v(11.93, 3.62) * mm});
            skLineSegment(sketch, "E360", {"start": v(11.93, 3.62) * mm, "end": v(11.93, 3.76) * mm});
            skLineSegment(sketch, "E361", {"start": v(11.93, 3.76) * mm, "end": v(11.93, 3.9) * mm});
            skLineSegment(sketch, "E362", {"start": v(11.93, 3.9) * mm, "end": v(12.07, 4.34) * mm});
            skLineSegment(sketch, "E363", {"start": v(12.07, 4.34) * mm, "end": v(12.43, 4.79) * mm});
            skLineSegment(sketch, "E364", {"start": v(12.43, 4.79) * mm, "end": v(12.94, 5.08) * mm});
            skLineSegment(sketch, "E365", {"start": v(12.94, 5.08) * mm, "end": v(13.4, 5.19) * mm});
            skLineSegment(sketch, "E366", {"start": v(13.4, 5.19) * mm, "end": v(13.54, 5.19) * mm});
            skLineSegment(sketch, "E367", {"start": v(31, -1.68) * mm, "end": v(26.74, -1.68) * mm});
            skLineSegment(sketch, "E368", {"start": v(26.74, -1.68) * mm, "end": v(26.74, -1.93) * mm});
            skLineSegment(sketch, "E369", {"start": v(26.74, -1.93) * mm, "end": v(26.72, -2.48) * mm});
            skLineSegment(sketch, "E370", {"start": v(26.72, -2.48) * mm, "end": v(26.72, -2.66) * mm});
            skLineSegment(sketch, "E371", {"start": v(26.72, -2.66) * mm, "end": v(26.72, -2.88) * mm});
            skLineSegment(sketch, "E372", {"start": v(26.72, -2.88) * mm, "end": v(26.75, -3.56) * mm});
            skLineSegment(sketch, "E373", {"start": v(26.75, -3.56) * mm, "end": v(26.93, -4.5) * mm});
            skLineSegment(sketch, "E374", {"start": v(26.93, -4.5) * mm, "end": v(27.4, -5.24) * mm});
            skLineSegment(sketch, "E375", {"start": v(27.4, -5.24) * mm, "end": v(28.05, -5.54) * mm});
            skLineSegment(sketch, "E376", {"start": v(28.05, -5.54) * mm, "end": v(28.27, -5.54) * mm});
            skLineSegment(sketch, "E377", {"start": v(28.27, -5.54) * mm, "end": v(28.51, -5.54) * mm});
            skLineSegment(sketch, "E378", {"start": v(28.51, -5.54) * mm, "end": v(29.25, -5.3) * mm});
            skLineSegment(sketch, "E379", {"start": v(29.25, -5.3) * mm, "end": v(30.06, -4.69) * mm});
            skLineSegment(sketch, "E380", {"start": v(30.06, -4.69) * mm, "end": v(30.6, -3.82) * mm});
            skLineSegment(sketch, "E381", {"start": v(30.6, -3.82) * mm, "end": v(30.81, -3.07) * mm});
            skLineSegment(sketch, "E382", {"start": v(30.81, -3.07) * mm, "end": v(30.82, -2.82) * mm});
            skLineSegment(sketch, "E383", {"start": v(30.82, -2.82) * mm, "end": v(31, -2.82) * mm});
            skLineSegment(sketch, "E384", {"start": v(31, -2.82) * mm, "end": v(30.98, -3.13) * mm});
            skLineSegment(sketch, "E385", {"start": v(30.98, -3.13) * mm, "end": v(30.7, -4.02) * mm});
            skLineSegment(sketch, "E386", {"start": v(30.7, -4.02) * mm, "end": v(29.99, -4.95) * mm});
            skLineSegment(sketch, "E387", {"start": v(29.99, -4.95) * mm, "end": v(28.98, -5.56) * mm});
            skLineSegment(sketch, "E388", {"start": v(28.98, -5.56) * mm, "end": v(28.06, -5.78) * mm});
            skLineSegment(sketch, "E389", {"start": v(28.06, -5.78) * mm, "end": v(27.76, -5.78) * mm});
            skLineSegment(sketch, "E390", {"start": v(27.76, -5.78) * mm, "end": v(27.36, -5.78) * mm});
            skLineSegment(sketch, "E391", {"start": v(27.36, -5.78) * mm, "end": v(26.18, -5.48) * mm});
            skLineSegment(sketch, "E392", {"start": v(26.18, -5.48) * mm, "end": v(24.9, -4.64) * mm});
            skLineSegment(sketch, "E393", {"start": v(24.9, -4.64) * mm, "end": v(24.07, -3.38) * mm});
            skLineSegment(sketch, "E394", {"start": v(24.07, -3.38) * mm, "end": v(23.76, -2.2) * mm});
            skLineSegment(sketch, "E395", {"start": v(23.76, -2.2) * mm, "end": v(23.76, -1.8) * mm});
            skLineSegment(sketch, "E396", {"start": v(23.76, -1.8) * mm, "end": v(23.76, -1.42) * mm});
            skLineSegment(sketch, "E397", {"start": v(23.76, -1.42) * mm, "end": v(24.05, -0.27) * mm});
            skLineSegment(sketch, "E398", {"start": v(24.05, -0.27) * mm, "end": v(24.86, 1) * mm});
            skLineSegment(sketch, "E399", {"start": v(24.86, 1) * mm, "end": v(26.08, 1.84) * mm});
            skLineSegment(sketch, "E400", {"start": v(26.08, 1.84) * mm, "end": v(27.23, 2.15) * mm});
            skLineSegment(sketch, "E401", {"start": v(27.23, 2.15) * mm, "end": v(27.61, 2.15) * mm});
            skLineSegment(sketch, "E402", {"start": v(27.61, 2.15) * mm, "end": v(27.95, 2.15) * mm});
            skLineSegment(sketch, "E403", {"start": v(27.95, 2.15) * mm, "end": v(28.98, 1.87) * mm});
            skLineSegment(sketch, "E404", {"start": v(28.98, 1.87) * mm, "end": v(30.05, 1.1) * mm});
            skLineSegment(sketch, "E405", {"start": v(30.05, 1.1) * mm, "end": v(30.75, -0.03) * mm});
            skLineSegment(sketch, "E406", {"start": v(30.75, -0.03) * mm, "end": v(31, -1.06) * mm});
            skLineSegment(sketch, "E407", {"start": v(31, -1.06) * mm, "end": v(31, -1.4) * mm});
            skLineSegment(sketch, "E408", {"start": v(31, -1.4) * mm, "end": v(31, -1.47) * mm});
            skLineSegment(sketch, "E409", {"start": v(31, -1.47) * mm, "end": v(31, -1.63) * mm});
            skLineSegment(sketch, "E410", {"start": v(31, -1.63) * mm, "end": v(31, -1.68) * mm});
            skLineSegment(sketch, "E411", {"start": v(18.78, -2.66) * mm, "end": v(18.84, -3.7) * mm});
            skLineSegment(sketch, "E412", {"start": v(18.84, -3.7) * mm, "end": v(18.85, -3.8) * mm});
            skLineSegment(sketch, "E413", {"start": v(18.85, -3.8) * mm, "end": v(18.86, -4.09) * mm});
            skLineSegment(sketch, "E414", {"start": v(18.86, -4.09) * mm, "end": v(18.92, -4.58) * mm});
            skLineSegment(sketch, "E415", {"start": v(18.92, -4.58) * mm, "end": v(19.09, -5) * mm});
            skLineSegment(sketch, "E416", {"start": v(19.09, -5) * mm, "end": v(19.35, -5.2) * mm});
            skLineSegment(sketch, "E417", {"start": v(19.35, -5.2) * mm, "end": v(19.44, -5.2) * mm});
            skLineSegment(sketch, "E418", {"start": v(19.44, -5.2) * mm, "end": v(19.52, -5.2) * mm});
            skLineSegment(sketch, "E419", {"start": v(19.52, -5.2) * mm, "end": v(19.79, -5.06) * mm});
            skLineSegment(sketch, "E420", {"start": v(19.79, -5.06) * mm, "end": v(20.04, -4.73) * mm});
            skLineSegment(sketch, "E421", {"start": v(20.04, -4.73) * mm, "end": v(20.2, -4.24) * mm});
            skLineSegment(sketch, "E422", {"start": v(20.2, -4.24) * mm, "end": v(20.29, -3.67) * mm});
            skLineSegment(sketch, "E423", {"start": v(20.29, -3.67) * mm, "end": v(20.33, -3.07) * mm});
            skLineSegment(sketch, "E424", {"start": v(20.33, -3.07) * mm, "end": v(20.33, -2.5) * mm});
            skLineSegment(sketch, "E425", {"start": v(20.33, -2.5) * mm, "end": v(20.32, -2.02) * mm});
            skLineSegment(sketch, "E426", {"start": v(20.32, -2.02) * mm, "end": v(20.31, -1.78) * mm});
            skLineSegment(sketch, "E427", {"start": v(20.31, -1.78) * mm, "end": v(20.31, -1.7) * mm});
            skLineSegment(sketch, "E428", {"start": v(20.31, -1.7) * mm, "end": v(20.31, -1.62) * mm});
            skLineSegment(sketch, "E429", {"start": v(20.31, -1.62) * mm, "end": v(20.32, -1.38) * mm});
            skLineSegment(sketch, "E430", {"start": v(20.32, -1.38) * mm, "end": v(20.33, -0.9) * mm});
            skLineSegment(sketch, "E431", {"start": v(20.33, -0.9) * mm, "end": v(20.33, -0.32) * mm});
            skLineSegment(sketch, "E432", {"start": v(20.33, -0.32) * mm, "end": v(20.29, 0.28) * mm});
            skLineSegment(sketch, "E433", {"start": v(20.29, 0.28) * mm, "end": v(20.2, 0.86) * mm});
            skLineSegment(sketch, "E434", {"start": v(20.2, 0.86) * mm, "end": v(20.04, 1.34) * mm});
            skLineSegment(sketch, "E435", {"start": v(20.04, 1.34) * mm, "end": v(19.79, 1.68) * mm});
            skLineSegment(sketch, "E436", {"start": v(19.79, 1.68) * mm, "end": v(19.52, 1.8) * mm});
            skLineSegment(sketch, "E437", {"start": v(19.52, 1.8) * mm, "end": v(19.44, 1.8) * mm});
            skLineSegment(sketch, "E438", {"start": v(19.44, 1.8) * mm, "end": v(19.35, 1.8) * mm});
            skLineSegment(sketch, "E439", {"start": v(19.35, 1.8) * mm, "end": v(19.09, 1.62) * mm});
            skLineSegment(sketch, "E440", {"start": v(19.09, 1.62) * mm, "end": v(18.92, 1.2) * mm});
            skLineSegment(sketch, "E441", {"start": v(18.92, 1.2) * mm, "end": v(18.86, 0.7) * mm});
            skLineSegment(sketch, "E442", {"start": v(18.86, 0.7) * mm, "end": v(18.85, 0.4) * mm});
            skLineSegment(sketch, "E443", {"start": v(18.85, 0.4) * mm, "end": v(18.84, 0.32) * mm});
            skLineSegment(sketch, "E444", {"start": v(18.84, 0.32) * mm, "end": v(18.78, -0.72) * mm});
            skLineSegment(sketch, "E445", {"start": v(18.78, -0.72) * mm, "end": v(18.78, -0.8) * mm});
            skLineSegment(sketch, "E446", {"start": v(18.78, -0.8) * mm, "end": v(18.76, -1.48) * mm});
            skLineSegment(sketch, "E447", {"start": v(18.76, -1.48) * mm, "end": v(18.76, -1.7) * mm});
            skLineSegment(sketch, "E448", {"start": v(18.76, -1.7) * mm, "end": v(18.76, -1.94) * mm});
            skLineSegment(sketch, "E449", {"start": v(18.76, -1.94) * mm, "end": v(18.78, -2.58) * mm});
            skLineSegment(sketch, "E450", {"start": v(18.78, -2.58) * mm, "end": v(18.78, -2.66) * mm});
            skLineSegment(sketch, "E451", {"start": v(-4.24, -1.5) * mm, "end": v(-4.24, -0.72) * mm});
            skLineSegment(sketch, "E452", {"start": v(-4.24, -0.72) * mm, "end": v(-4.24, -0.15) * mm});
            skLineSegment(sketch, "E453", {"start": v(-4.24, -0.15) * mm, "end": v(-4.24, 0.21) * mm});
            skLineSegment(sketch, "E454", {"start": v(-4.24, 0.21) * mm, "end": v(-4.24, 0.34) * mm});
            skLineSegment(sketch, "E455", {"start": v(-4.24, 0.34) * mm, "end": v(-4.25, 0.7) * mm});
            skLineSegment(sketch, "E456", {"start": v(-4.25, 0.7) * mm, "end": v(-4.32, 1.27) * mm});
            skLineSegment(sketch, "E457", {"start": v(-4.32, 1.27) * mm, "end": v(-4.54, 1.76) * mm});
            skLineSegment(sketch, "E458", {"start": v(-4.54, 1.76) * mm, "end": v(-4.87, 1.97) * mm});
            skLineSegment(sketch, "E459", {"start": v(-4.87, 1.97) * mm, "end": v(-4.98, 1.97) * mm});
            skLineSegment(sketch, "E460", {"start": v(-4.98, 1.97) * mm, "end": v(-5.07, 1.97) * mm});
            skLineSegment(sketch, "E461", {"start": v(-5.07, 1.97) * mm, "end": v(-5.33, 1.85) * mm});
            skLineSegment(sketch, "E462", {"start": v(-5.33, 1.85) * mm, "end": v(-5.57, 1.53) * mm});
            skLineSegment(sketch, "E463", {"start": v(-5.57, 1.53) * mm, "end": v(-5.74, 1.07) * mm});
            skLineSegment(sketch, "E464", {"start": v(-5.74, 1.07) * mm, "end": v(-5.83, 0.51) * mm});
            skLineSegment(sketch, "E465", {"start": v(-5.83, 0.51) * mm, "end": v(-5.88, -0.08) * mm});
            skLineSegment(sketch, "E466", {"start": v(-5.88, -0.08) * mm, "end": v(-5.89, -0.65) * mm});
            skLineSegment(sketch, "E467", {"start": v(-5.89, -0.65) * mm, "end": v(-5.88, -1.14) * mm});
            skLineSegment(sketch, "E468", {"start": v(-5.88, -1.14) * mm, "end": v(-5.87, -1.4) * mm});
            skLineSegment(sketch, "E469", {"start": v(-5.87, -1.4) * mm, "end": v(-5.87, -1.5) * mm});
            skLineSegment(sketch, "E470", {"start": v(-5.87, -1.5) * mm, "end": v(-4.24, -1.5) * mm});
            skLineSegment(sketch, "E471", {"start": v(-27.55, -0.64) * mm, "end": v(-24.66, -0.64) * mm});
            skLineSegment(sketch, "E472", {"start": v(-24.66, -0.64) * mm, "end": v(-26.13, 3.99) * mm});
            skLineSegment(sketch, "E473", {"start": v(-26.13, 3.99) * mm, "end": v(-27.55, -0.64) * mm});
            skLineSegment(sketch, "E474", {"start": v(28.37, -1.5) * mm, "end": v(28.35, -0.72) * mm});
            skLineSegment(sketch, "E475", {"start": v(28.35, -0.72) * mm, "end": v(28.35, -0.15) * mm});
            skLineSegment(sketch, "E476", {"start": v(28.35, -0.15) * mm, "end": v(28.35, 0.21) * mm});
            skLineSegment(sketch, "E477", {"start": v(28.35, 0.21) * mm, "end": v(28.35, 0.34) * mm});
            skLineSegment(sketch, "E478", {"start": v(28.35, 0.34) * mm, "end": v(28.34, 0.7) * mm});
            skLineSegment(sketch, "E479", {"start": v(28.34, 0.7) * mm, "end": v(28.27, 1.27) * mm});
            skLineSegment(sketch, "E480", {"start": v(28.27, 1.27) * mm, "end": v(28.06, 1.76) * mm});
            skLineSegment(sketch, "E481", {"start": v(28.06, 1.76) * mm, "end": v(27.74, 1.97) * mm});
            skLineSegment(sketch, "E482", {"start": v(27.74, 1.97) * mm, "end": v(27.63, 1.97) * mm});
            skLineSegment(sketch, "E483", {"start": v(27.63, 1.97) * mm, "end": v(27.54, 1.97) * mm});
            skLineSegment(sketch, "E484", {"start": v(27.54, 1.97) * mm, "end": v(27.28, 1.85) * mm});
            skLineSegment(sketch, "E485", {"start": v(27.28, 1.85) * mm, "end": v(27.03, 1.53) * mm});
            skLineSegment(sketch, "E486", {"start": v(27.03, 1.53) * mm, "end": v(26.86, 1.07) * mm});
            skLineSegment(sketch, "E487", {"start": v(26.86, 1.07) * mm, "end": v(26.76, 0.51) * mm});
            skLineSegment(sketch, "E488", {"start": v(26.76, 0.51) * mm, "end": v(26.72, -0.08) * mm});
            skLineSegment(sketch, "E489", {"start": v(26.72, -0.08) * mm, "end": v(26.7, -0.65) * mm});
            skLineSegment(sketch, "E490", {"start": v(26.7, -0.65) * mm, "end": v(26.7, -1.14) * mm});
            skLineSegment(sketch, "E491", {"start": v(26.7, -1.14) * mm, "end": v(26.72, -1.4) * mm});
            skLineSegment(sketch, "E492", {"start": v(26.72, -1.4) * mm, "end": v(26.72, -1.5) * mm});
            skLineSegment(sketch, "E493", {"start": v(26.72, -1.5) * mm, "end": v(28.37, -1.5) * mm});
            skSolve(sketch);
        }
        {
            var Q0;
            Q0=makeQuery(id+"F5.imprint","IMPRINT",FACE,{"disambiguationData":[TD([[makeQuery(id+"F5.imprint","IMPRINT",EDGE,{"derivedFrom":sQuery(id+"F5.wireOp",EDGE,"E157")}),-1.0]])]});
            var Q1;
            Q1=makeQuery(id+"F5.imprint","IMPRINT",FACE,{"disambiguationData":[TD([[makeQuery(id+"F5.imprint","IMPRINT",EDGE,{"derivedFrom":sQuery(id+"F5.wireOp",EDGE,"E121")}),-1.0]])]});
            var Q2;
            Q2=makeQuery(id+"F5.imprint","IMPRINT",FACE,{"disambiguationData":[TD([[makeQuery(id+"F5.imprint","IMPRINT",EDGE,{"derivedFrom":sQuery(id+"F5.wireOp",EDGE,"E260")}),-1.0]])]});
            var Q3;
            Q3=makeQuery(id+"F5.imprint","IMPRINT",FACE,{"disambiguationData":[TD([[makeQuery(id+"F5.imprint","IMPRINT",EDGE,{"derivedFrom":sQuery(id+"F5.wireOp",EDGE,"E2")}),-1.0]])]});
            var Q4;
            Q4=makeQuery(id+"F5.imprint","IMPRINT",FACE,{"disambiguationData":[TD([[makeQuery(id+"F5.imprint","IMPRINT",EDGE,{"derivedFrom":sQuery(id+"F5.wireOp",EDGE,"E99")}),-1.0]])]});
            var Q5;
            Q5=makeQuery(id+"F5.imprint","IMPRINT",FACE,{"disambiguationData":[TD([[makeQuery(id+"F5.imprint","IMPRINT",EDGE,{"derivedFrom":sQuery(id+"F5.wireOp",EDGE,"E343")}),-1.0]])]});
            var Q6;
            Q6=makeQuery(id+"F5.imprint","IMPRINT",FACE,{"disambiguationData":[TD([[makeQuery(id+"F5.imprint","IMPRINT",EDGE,{"derivedFrom":sQuery(id+"F5.wireOp",EDGE,"E304")}),-1.0]])]});
            var Q7;
            Q7=makeQuery(id+"F5.imprint","IMPRINT",FACE,{"disambiguationData":[TD([[makeQuery(id+"F5.imprint","IMPRINT",EDGE,{"derivedFrom":sQuery(id+"F5.wireOp",EDGE,"E367")}),-1.0]])]});
            extrude(context, id + "F6", {"entities" : qUnion([Q0, Q1, Q2, Q3, Q4, Q5, Q6, Q7]), "operationType" : NewBodyOperationType.ADD, "depth" : 2 * mm, "offsetDistance" : 25 * mm});
        }
    });
